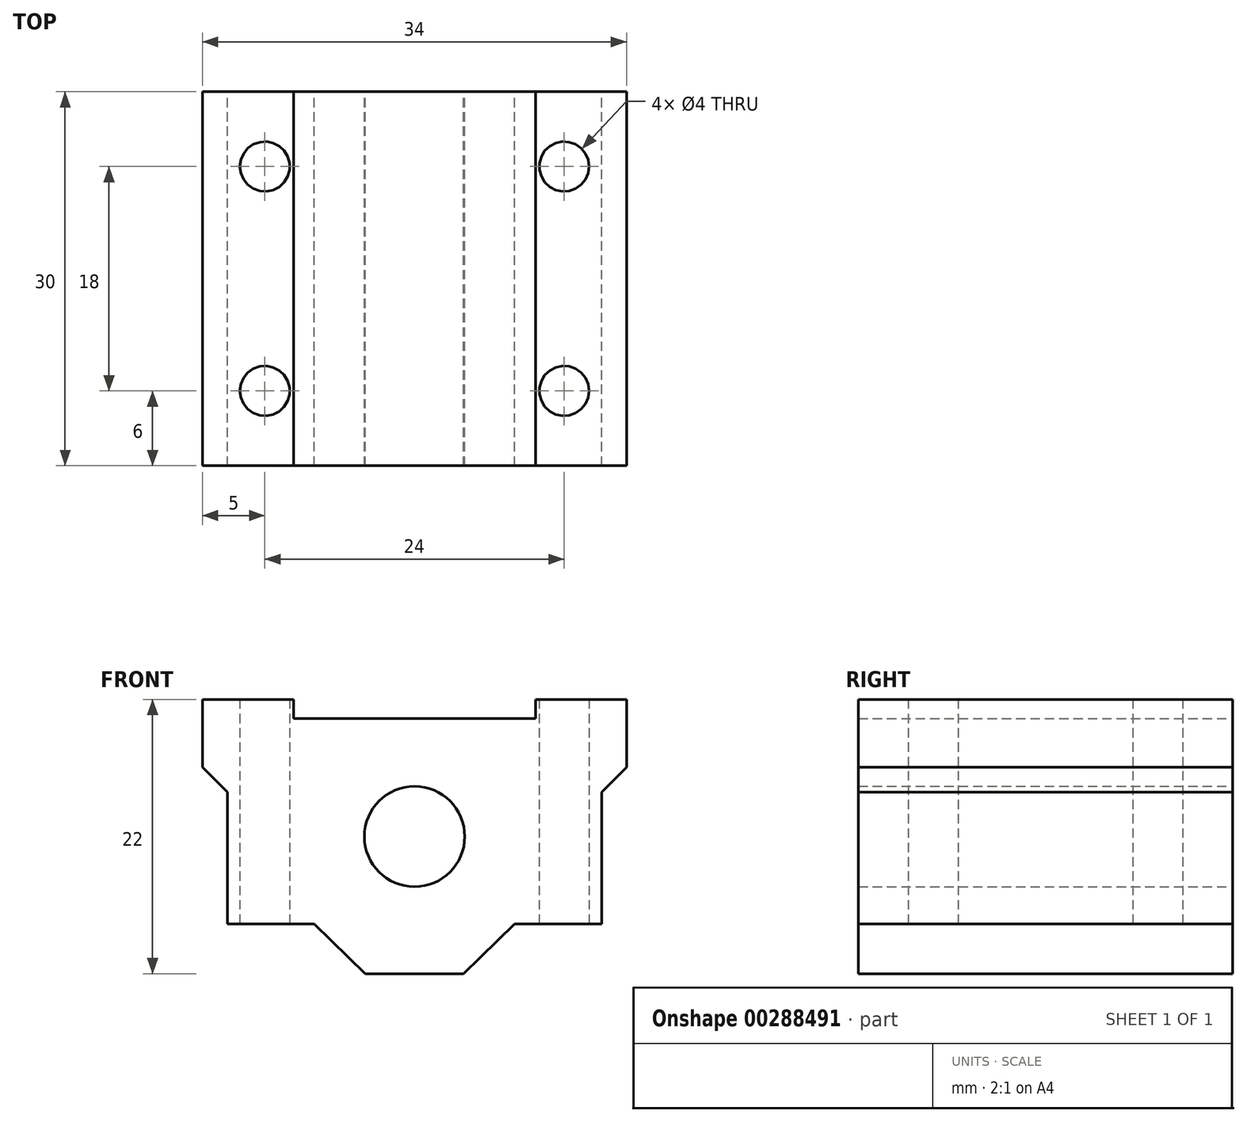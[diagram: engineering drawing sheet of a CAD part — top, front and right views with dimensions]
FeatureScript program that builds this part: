
annotation { "Feature Type Name" : "Feature", "Feature Type Description" : "" }
export const myFeature = defineFeature(function(context is Context, id is Id, definition is map)
    precondition{}
    {
        {
            var Q0;
            Q0=qCreatedBy(makeId("Front.planeOp"),FACE);
            var sketch = newSketch(context, id + "F0", { "sketchPlane" : qUnion([Q0])});
            skLineSegment(sketch, "E0.right", {"start": v(-17, 5.57) * mm, "end": v(-17, 11) * mm});
            skPoint(sketch, "E0.middle", {"position": v(0, 0) * mm});
            skLineSegment(sketch, "E1.right", {"start": v(-9.7, 9.47) * mm, "end": v(-9.7, 11) * mm});
            skPoint(sketch, "E1.middle", {"position": v(0, 11) * mm});
            skLineSegment(sketch, "E2.right", {"start": v(-15, 3.57) * mm, "end": v(-15, -7) * mm});
            skPoint(sketch, "E3.middle", {"position": v(0, -11) * mm});
            skPoint(sketch, "E4.orphan", {"position": v(-9.7, 12.53) * mm});
            skLineSegment(sketch, "E5.trimOffspring", {"start": v(-9.7, 11) * mm, "end": v(-17, 11) * mm});
            skPoint(sketch, "E6.orphan", {"position": v(9.7, 12.53) * mm});
            skPoint(sketch, "E7.orphan", {"position": v(-17, -11) * mm});
            skLineSegment(sketch, "E8", {"start": v(-17, 5.57) * mm, "end": v(-15, 3.57) * mm});
            skLineSegment(sketch, "E9", {"start": v(-8.03, -7) * mm, "end": v(-3.94, -11) * mm});
            skLineSegment(sketch, "E10", {"start": v(0, 9.47) * mm, "end": v(-9.7, 9.47) * mm});
            skLineSegment(sketch, "E11", {"start": v(0, -11) * mm, "end": v(-3.94, -11) * mm});
            skPoint(sketch, "E0.left.start.orphan", {"position": v(17, -11) * mm});
            skPoint(sketch, "E0.top.start.orphan", {"position": v(17, 11) * mm});
            skPoint(sketch, "E1.left.start.orphan", {"position": v(9.7, 9.47) * mm});
            skPoint(sketch, "E3.bottom.start.orphan", {"position": v(3.94, -11) * mm});
            skPoint(sketch, "E3.top.start.orphan", {"position": v(3.94, -11) * mm});
            skLineSegment(sketch, "E12.trimOffspring", {"start": v(-8.03, -7) * mm, "end": v(-15, -7) * mm});
            skPoint(sketch, "E13.end.orphan", {"position": v(-3.94, -11) * mm});
            skLineSegment(sketch, "E14.MirrorCS", {"start": v(9.7, 9.47) * mm, "end": v(9.7, 11) * mm});
            skLineSegment(sketch, "E15.MirrorCS", {"start": v(9.7, 11) * mm, "end": v(17, 11) * mm});
            skLineSegment(sketch, "E16.MirrorCS", {"start": v(17, 5.57) * mm, "end": v(15, 3.57) * mm});
            skLineSegment(sketch, "E17.MirrorCS", {"start": v(15, 3.57) * mm, "end": v(15, -7) * mm});
            skLineSegment(sketch, "E18.MirrorCS", {"start": v(8.03, -7) * mm, "end": v(15, -7) * mm});
            skLineSegment(sketch, "E19.MirrorCS", {"start": v(17, 5.57) * mm, "end": v(17, 11) * mm});
            skLineSegment(sketch, "E20.MirrorCS", {"start": v(8.03, -7) * mm, "end": v(3.94, -11) * mm});
            skLineSegment(sketch, "E21", {"start": v(9.7, 9.47) * mm, "end": v(0, 9.47) * mm});
            skLineSegment(sketch, "E22", {"start": v(3.94, -11) * mm, "end": v(0, -11) * mm});
            skCircle(sketch, "E23", {"center": v(0, 0) * mm, "radius": 4.03 * mm});
            skSolve(sketch);
        }
        {
            var Q0;
            Q0 = qSketchRegion(id + "F0", true);
            extrude(context, id + "F1", {"entities" : qUnion([Q0]), "depth" : 30 * mm});
        }
        {
            var Q0;
            Q0=qCreatedBy(makeId("Top.planeOp"),FACE);
            var sketch = newSketch(context, id + "F2", { "sketchPlane" : qUnion([Q0])});
            skCircle(sketch, "E24", {"center": v(-12, -6) * mm, "radius": 2 * mm});
            skCircle(sketch, "E25", {"center": v(-12, -24) * mm, "radius": 2 * mm});
            skLineSegment(sketch, "E26", {"start": v(0, 8) * mm, "end": v(0, -42.82) * mm, "construction": true});
            skCircle(sketch, "E27.MirrorC", {"center": v(12, -6) * mm, "radius": 2 * mm});
            skCircle(sketch, "E28.MirrorC", {"center": v(12, -24) * mm, "radius": 2 * mm});
            skSolve(sketch);
        }
        {
            var Q0;
            Q0 = qSketchRegion(id + "F2", true);
            extrude(context, id + "F3", {"entities" : qUnion([Q0]), "operationType" : NewBodyOperationType.REMOVE, "endBound" : BoundingType.UP_TO_NEXT, "depth" : 25 * mm, "hasSecondDirection" : true, "secondDirectionOppositeDirection" : true, "secondDirectionDepth" : 25 * mm});
        }
    });
